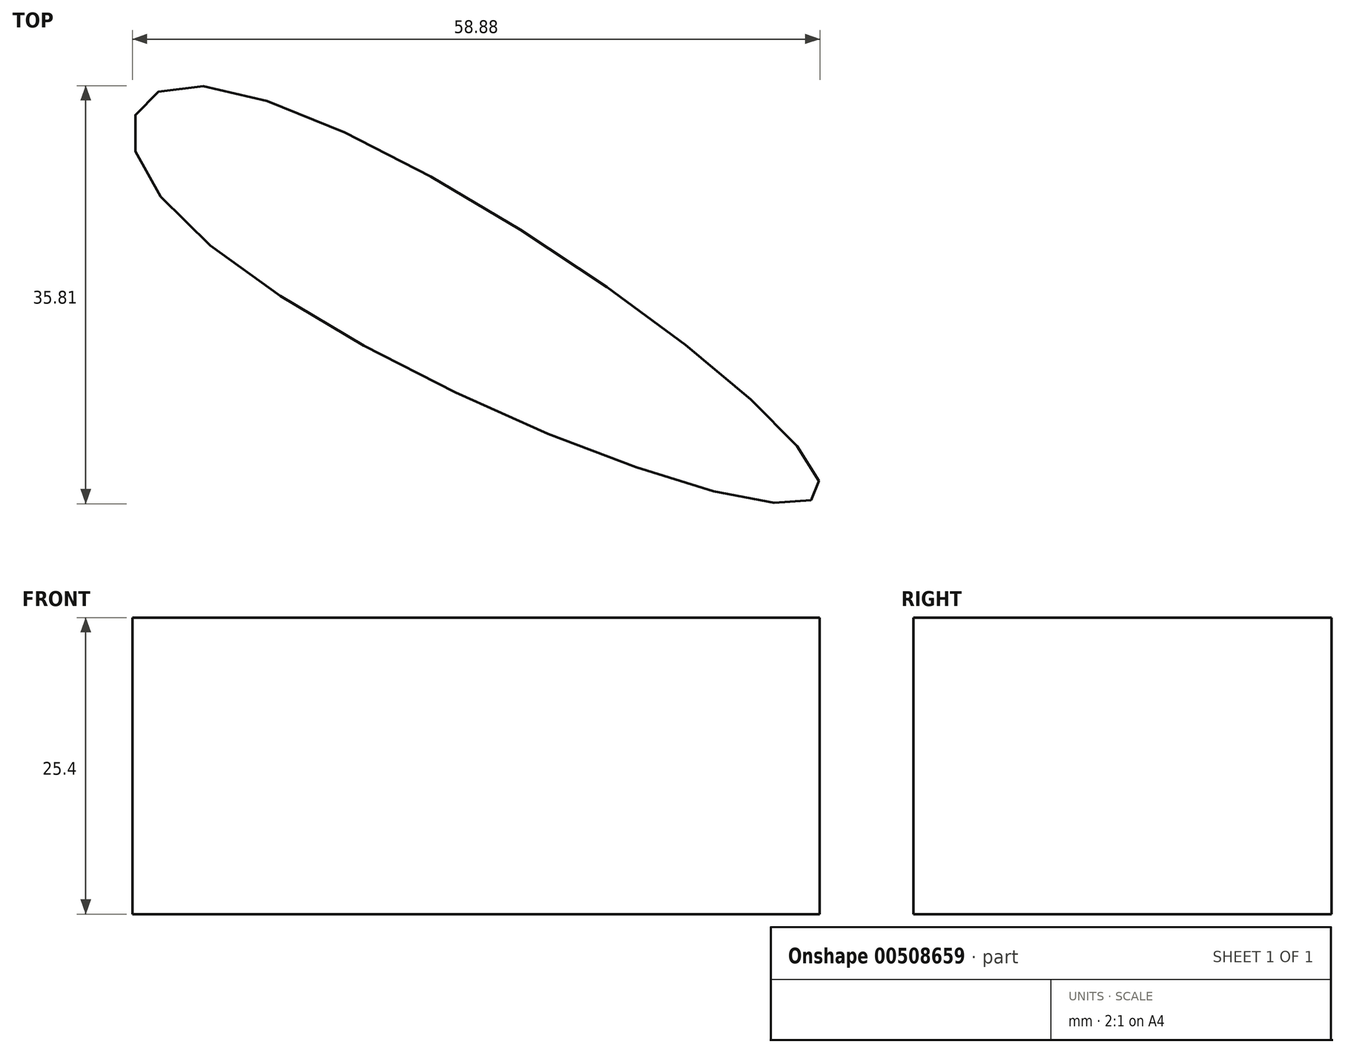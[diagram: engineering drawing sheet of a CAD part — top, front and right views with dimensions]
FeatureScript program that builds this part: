
annotation { "Feature Type Name" : "Feature", "Feature Type Description" : "" }
export const myFeature = defineFeature(function(context is Context, id is Id, definition is map)
    precondition{}
    {
        {
            var Q0;
            Q0=qCreatedBy(makeId("Top.planeOp"),FACE);
            var sketch = newSketch(context, id + "F0", { "sketchPlane" : qUnion([Q0])});
            skFitSpline(sketch, "E0", {"points": [v(-30.2, 0) * mm, v(26.21, -25.35) * mm, v(-27.42, 9.5) * mm, v(-30.2, 0) * mm]});
            skSolve(sketch);
        }
        {
            var Q0;
            Q0 = qSketchRegion(id + "F0", true);
            extrude(context, id + "F1", {"entities" : qUnion([Q0]), "depth" : 25.4 * mm});
        }
    });
